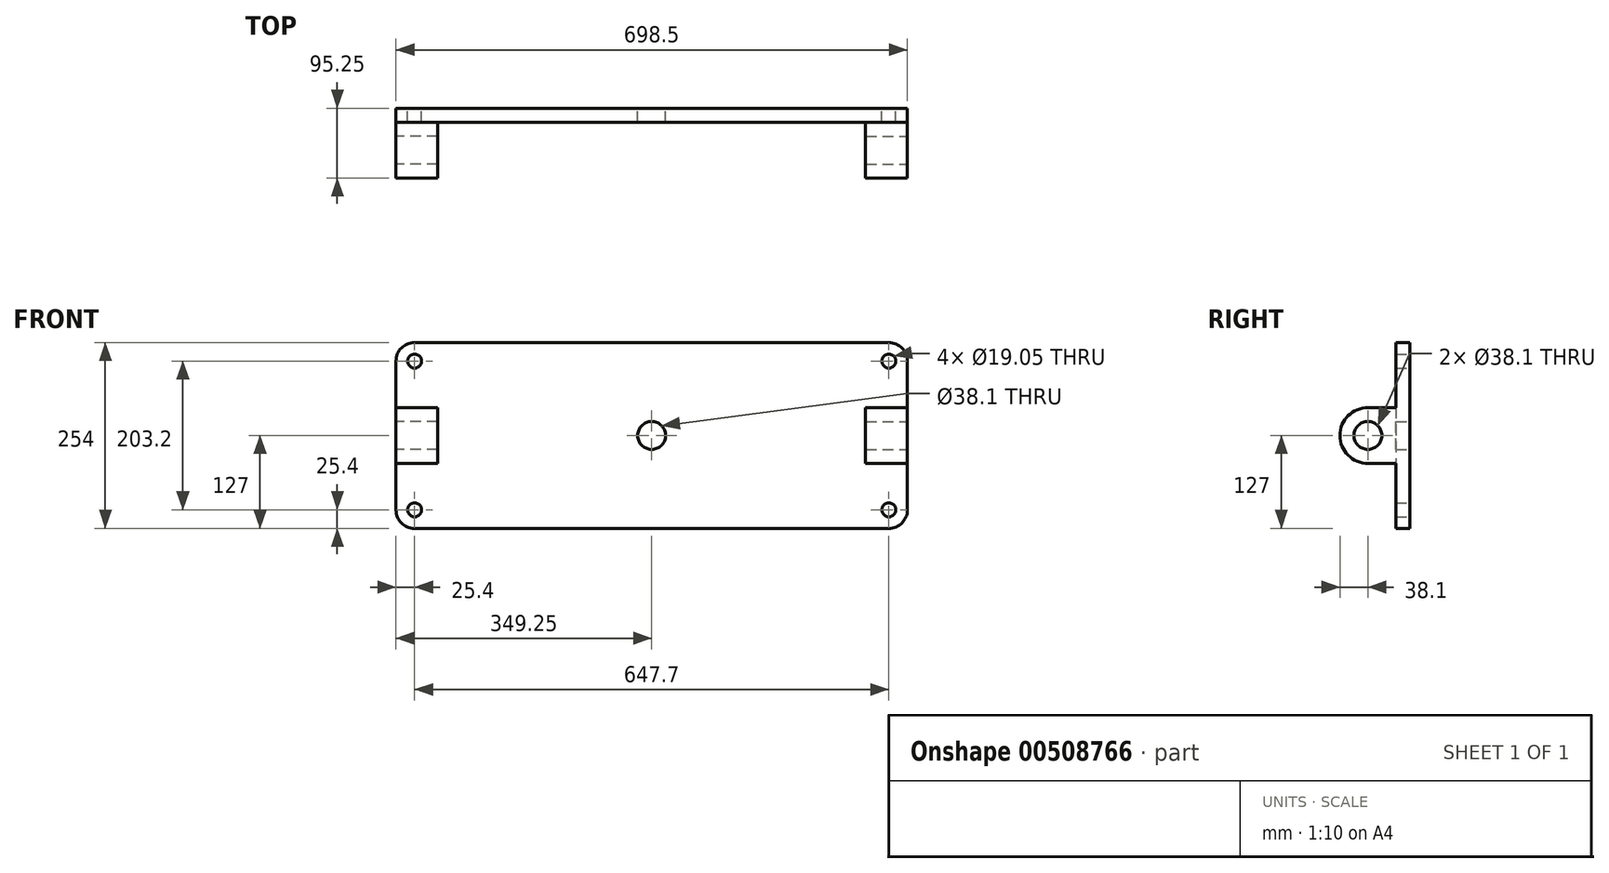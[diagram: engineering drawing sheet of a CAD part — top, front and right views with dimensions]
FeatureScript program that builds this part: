
annotation { "Feature Type Name" : "Feature", "Feature Type Description" : "" }
export const myFeature = defineFeature(function(context is Context, id is Id, definition is map)
    precondition{}
    {
        {
            var Q0;
            Q0=qCreatedBy(makeId("Front.planeOp"),FACE);
            var sketch = newSketch(context, id + "F0", { "sketchPlane" : qUnion([Q0])});
            skLineSegment(sketch, "E0.bottom", {"start": v(-323.85, 127) * mm, "end": v(323.85, 127) * mm});
            skLineSegment(sketch, "E0.top", {"start": v(-323.85, -127) * mm, "end": v(323.85, -127) * mm});
            skLineSegment(sketch, "E0.left", {"start": v(-349.25, 101.6) * mm, "end": v(-349.25, -101.6) * mm});
            skLineSegment(sketch, "E0.right", {"start": v(349.25, 101.6) * mm, "end": v(349.25, -101.6) * mm});
            skPoint(sketch, "E0.middle", {"position": v(0, 0) * mm});
            skCircle(sketch, "E1", {"center": v(0, 0) * mm, "radius": 19.05 * mm});
            skCircle(sketch, "E2", {"center": v(-323.85, 101.6) * mm, "radius": 9.53 * mm});
            skCircle(sketch, "E3.MirrorC", {"center": v(323.85, 101.6) * mm, "radius": 9.53 * mm});
            skCircle(sketch, "E4.MirrorC", {"center": v(323.85, -101.6) * mm, "radius": 9.53 * mm});
            skCircle(sketch, "E5.MirrorC", {"center": v(-323.85, -101.6) * mm, "radius": 9.53 * mm});
            skPoint(sketch, "E6.visualSharp", {"position": v(-349.25, 127) * mm});
            skArc(sketch, "E6.filletArc", {"start": v(-323.85, 127) * mm, "mid": v(-341.81, 119.56) * mm, "end": v(-349.25, 101.6) * mm});
            skPoint(sketch, "E7.visualSharp", {"position": v(-349.25, -127) * mm});
            skArc(sketch, "E7.filletArc", {"start": v(-349.25, -101.6) * mm, "mid": v(-341.81, -119.56) * mm, "end": v(-323.85, -127) * mm});
            skPoint(sketch, "E8.visualSharp", {"position": v(349.25, -127) * mm});
            skArc(sketch, "E8.filletArc", {"start": v(323.85, -127) * mm, "mid": v(341.81, -119.56) * mm, "end": v(349.25, -101.6) * mm});
            skPoint(sketch, "E9.visualSharp", {"position": v(349.25, 127) * mm});
            skArc(sketch, "E9.filletArc", {"start": v(349.25, 101.6) * mm, "mid": v(341.81, 119.56) * mm, "end": v(323.85, 127) * mm});
            skSolve(sketch);
        }
        {
            var Q0;
            Q0=makeQuery(id+"F0.imprint","IMPRINT",FACE,{"disambiguationData":[TD([[makeQuery(id+"F0.imprint","IMPRINT",EDGE,{"derivedFrom":sQuery(id+"F0.wireOp",EDGE,"E0.bottom")}),-1.0]])]});
            extrude(context, id + "F1", {"entities" : qUnion([Q0]), "depth" : 19.05 * mm});
        }
        {
            var Q0;
            Q0=makeQuery(id+"F1.opExtrude","SWEPT_FACE",FACE,{"disambiguationData":[OSD([sQuery(id+"F0.wireOp",EDGE,"E0.right")])]});
            var sketch = newSketch(context, id + "F2", { "sketchPlane" : qUnion([Q0])});
            skCircle(sketch, "E10", {"center": v(-57.15, 0) * mm, "radius": 19.05 * mm});
            skLineSegment(sketch, "E11", {"start": v(-19.05, 38.1) * mm, "end": v(-57.15, 38.1) * mm});
            skLineSegment(sketch, "E12.MirrorCS", {"start": v(-19.05, -38.1) * mm, "end": v(-57.15, -38.1) * mm});
            skArc(sketch, "E13", {"start": v(-57.15, 38.1) * mm, "mid": v(-95.25, 0) * mm, "end": v(-57.15, -38.1) * mm});
            skSolve(sketch);
        }
        {
            var Q0;
            Q0=makeQuery(id+"F2.imprint","IMPRINT",FACE,{"disambiguationData":[TD([[makeQuery(id+"F2.imprint","IMPRINT",EDGE,{"derivedFrom":sQuery(id+"F2.wireOp",EDGE,"E10")}),-1.0]])]});
            extrude(context, id + "F3", {"entities" : qUnion([Q0]), "oppositeDirection" : true, "depth" : 57.15 * mm});
        }
        {
            var Q0;
            Q0=makeQuery(id+"F3.opExtrude","SWEPT_BODY",BODY,{"disambiguationData":[OSD([sQuery(id+"F0.wireOp",EDGE,"E0.right"),sQuery(id+"F2.wireOp",EDGE,"E10"),sQuery(id+"F2.wireOp",EDGE,"E11"),sQuery(id+"F2.wireOp",EDGE,"E12.MirrorCS"),sQuery(id+"F2.wireOp",EDGE,"E13")])]});
            var Q1;
            Q1=qCreatedBy(makeId("Right.planeOp"),FACE);
            mirror(context, id + "F4", {"operationType" : NewBodyOperationType.ADD, "entities" : qUnion([Q0]), "mirrorPlane" : qUnion([Q1])});
        }
    });
